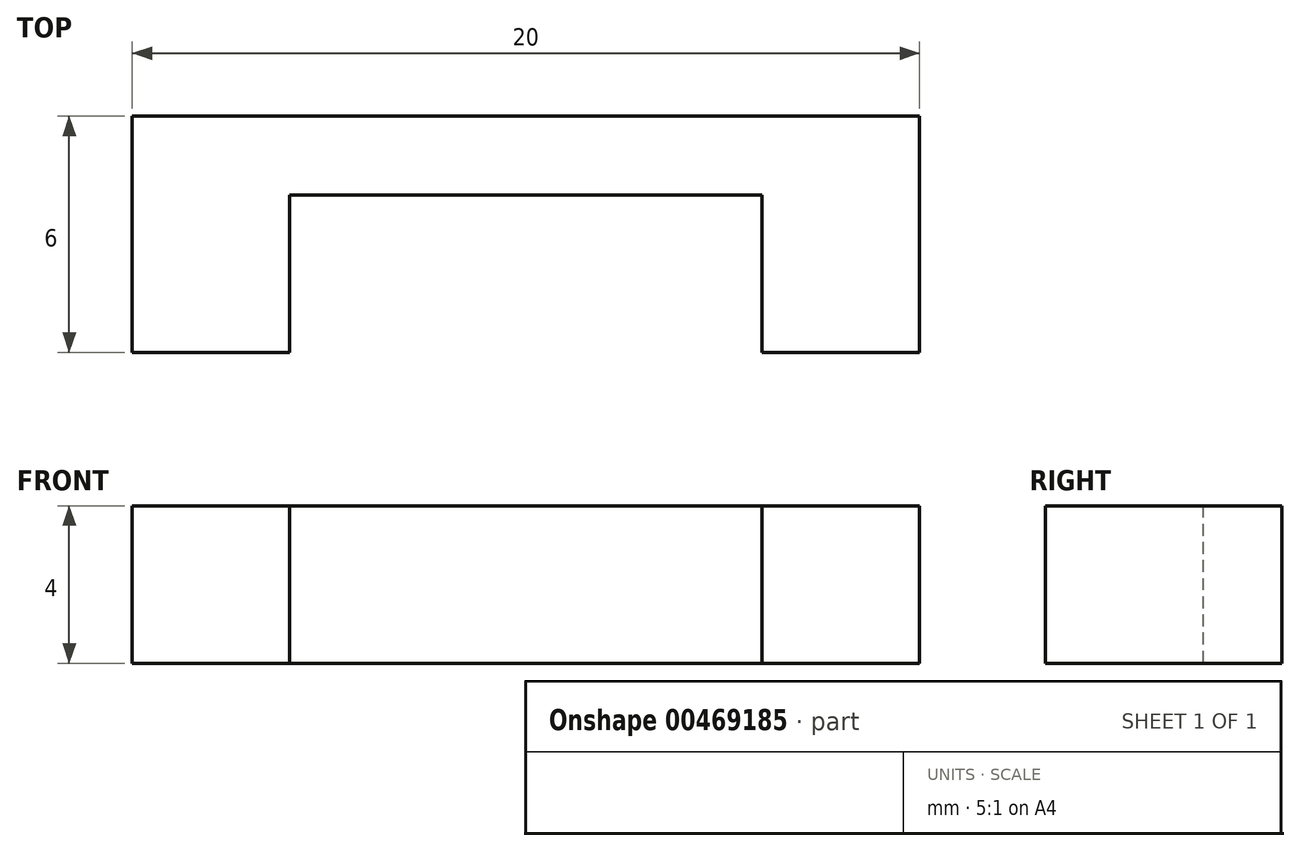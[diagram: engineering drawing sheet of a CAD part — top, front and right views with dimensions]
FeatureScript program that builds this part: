
annotation { "Feature Type Name" : "Feature", "Feature Type Description" : "" }
export const myFeature = defineFeature(function(context is Context, id is Id, definition is map)
    precondition{}
    {
        {
            var Q0;
            Q0=qCreatedBy(makeId("Front.planeOp"),FACE);
            var sketch = newSketch(context, id + "F0", { "sketchPlane" : qUnion([Q0])});
            skLineSegment(sketch, "E0.bottom", {"start": v(10, -2) * mm, "end": v(-10, -2) * mm});
            skLineSegment(sketch, "E0.top", {"start": v(10, 2) * mm, "end": v(-10, 2) * mm});
            skLineSegment(sketch, "E0.left", {"start": v(10, -2) * mm, "end": v(10, 2) * mm});
            skLineSegment(sketch, "E0.right", {"start": v(-10, -2) * mm, "end": v(-10, 2) * mm});
            skPoint(sketch, "E0.middle", {"position": v(0, 0) * mm});
            skSolve(sketch);
        }
        {
            var Q0;
            Q0=makeQuery(id+"F0.imprint","IMPRINT",FACE,{"disambiguationData":[TD([[makeQuery(id+"F0.imprint","IMPRINT",EDGE,{"derivedFrom":sQuery(id+"F0.wireOp",EDGE,"E0.bottom")}),-1.0]])]});
            extrude(context, id + "F1", {"entities" : qUnion([Q0]), "depth" : 2 * mm, "offsetDistance" : 25 * mm});
        }
        {
            var Q0;
            Q0=makeQuery(id+"F1.opExtrude","CAP_FACE",FACE,{"disambiguationData":[OSD([sQuery(id+"F0.wireOp",EDGE,"E0.bottom"),sQuery(id+"F0.wireOp",EDGE,"E0.top"),sQuery(id+"F0.wireOp",EDGE,"E0.left"),sQuery(id+"F0.wireOp",EDGE,"E0.right")])],"isStart":false});
            var sketch = newSketch(context, id + "F2", { "sketchPlane" : qUnion([Q0])});
            skLineSegment(sketch, "E1", {"start": v(-6, 2) * mm, "end": v(-6, -2) * mm});
            skLineSegment(sketch, "E2", {"start": v(6, 2) * mm, "end": v(6, -2) * mm});
            skSolve(sketch);
        }
        {
            var Q0;
            {var subQ0=sQuery(id+"F2.wireOp",EDGE,"E1");Q0=makeQuery(id+"F2.imprint","IMPRINT",FACE,{"disambiguationData":[TD([[makeQuery(id+"F2.imprint","IMPRINT",EDGE,{"derivedFrom":subQ0}),-1.0]])]});}
            var Q1;
            {var subQ0=sQuery(id+"F2.wireOp",EDGE,"E2");Q1=makeQuery(id+"F2.imprint","IMPRINT",FACE,{"disambiguationData":[TD([[makeQuery(id+"F2.imprint","IMPRINT",EDGE,{"derivedFrom":subQ0}),1.0]])]});}
            extrude(context, id + "F3", {"entities" : qUnion([Q0, Q1]), "operationType" : NewBodyOperationType.ADD, "depth" : 4 * mm, "offsetDistance" : 25 * mm});
        }
    });
